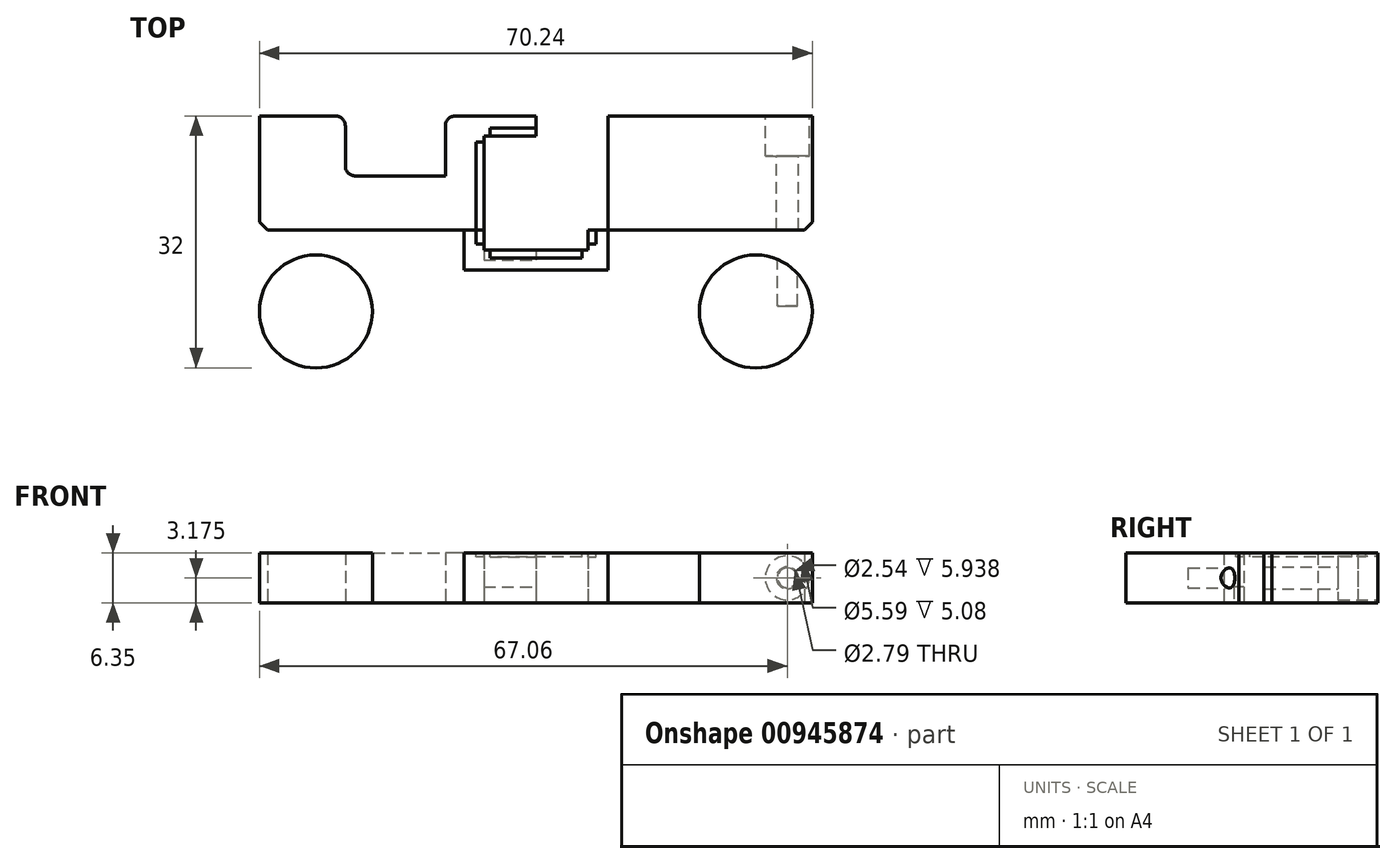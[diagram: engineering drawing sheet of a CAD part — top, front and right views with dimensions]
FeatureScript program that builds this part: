
annotation { "Feature Type Name" : "Feature", "Feature Type Description" : "" }
export const myFeature = defineFeature(function(context is Context, id is Id, definition is map)
    precondition{}
    {
        {
            var Q0;
            Q0=qCreatedBy(makeId("Top.planeOp"),FACE);
            var sketch = newSketch(context, id + "F0", { "sketchPlane" : qUnion([Q0])});
            skLineSegment(sketch, "E0", {"start": v(0, 0) * mm, "end": v(35.12, 0) * mm});
            skLineSegment(sketch, "E1", {"start": v(0, 0) * mm, "end": v(-35.12, 0) * mm});
            skLineSegment(sketch, "E2", {"start": v(0, 0) * mm, "end": v(0, -32) * mm});
            skLineSegment(sketch, "E3", {"start": v(0, 0) * mm, "end": v(0, -14.48) * mm});
            skLineSegment(sketch, "E4", {"start": v(35.12, 0) * mm, "end": v(35.12, -32) * mm});
            skLineSegment(sketch, "E5", {"start": v(-35.12, 0) * mm, "end": v(-35.12, -32) * mm});
            skLineSegment(sketch, "E6", {"start": v(-35.12, -32) * mm, "end": v(35.12, -32) * mm});
            skLineSegment(sketch, "E7", {"start": v(-35.12, -14.48) * mm, "end": v(-35.12, -15.5) * mm});
            skLineSegment(sketch, "E8", {"start": v(0, -32) * mm, "end": v(-27.94, -32) * mm});
            skLineSegment(sketch, "E9", {"start": v(0, -32) * mm, "end": v(27.94, -32) * mm});
            skLineSegment(sketch, "E10", {"start": v(-27.94, -32) * mm, "end": v(-27.94, -24.83) * mm});
            skLineSegment(sketch, "E11", {"start": v(27.94, -32) * mm, "end": v(27.94, -24.83) * mm});
            skCircle(sketch, "E12", {"center": v(-27.94, -24.83) * mm, "radius": 7.18 * mm});
            skCircle(sketch, "E13", {"center": v(27.94, -24.83) * mm, "radius": 7.18 * mm});
            skLineSegment(sketch, "E14", {"start": v(-35.12, 0) * mm, "end": v(-24.2, 0) * mm});
            skLineSegment(sketch, "E15", {"start": v(-24.2, 0) * mm, "end": v(-11.5, 0) * mm});
            skLineSegment(sketch, "E16", {"start": v(-11.5, 0) * mm, "end": v(-11.5, -7.62) * mm});
            skLineSegment(sketch, "E17.top", {"start": v(-24.2, -7.62) * mm, "end": v(-11.5, -7.62) * mm});
            skLineSegment(sketch, "E17.left", {"start": v(-24.2, 0) * mm, "end": v(-24.2, -7.62) * mm});
            skLineSegment(sketch, "E18", {"start": v(0, 0) * mm, "end": v(-6.6, 0) * mm});
            skLineSegment(sketch, "E19", {"start": v(-6.6, 0) * mm, "end": v(-9.14, 0) * mm});
            skLineSegment(sketch, "E20", {"start": v(-6.6, 0) * mm, "end": v(-6.6, -2.54) * mm});
            skLineSegment(sketch, "E21", {"start": v(-6.6, -2.54) * mm, "end": v(0, -2.54) * mm});
            skLineSegment(sketch, "E22", {"start": v(0, -2.54) * mm, "end": v(6.6, -2.54) * mm});
            skLineSegment(sketch, "E23", {"start": v(6.6, -2.54) * mm, "end": v(6.6, -17.02) * mm});
            skLineSegment(sketch, "E24.bottom", {"start": v(-6.6, -2.54) * mm, "end": v(6.6, -2.54) * mm});
            skLineSegment(sketch, "E24.top", {"start": v(-6.6, -17.02) * mm, "end": v(6.6, -17.02) * mm});
            skLineSegment(sketch, "E24.left", {"start": v(-6.6, -2.54) * mm, "end": v(-6.6, -17.02) * mm});
            skLineSegment(sketch, "E25.bottom", {"start": v(6.6, -17.02) * mm, "end": v(9.14, -17.02) * mm});
            skLineSegment(sketch, "E25.top", {"start": v(6.6, -19.56) * mm, "end": v(9.14, -19.56) * mm});
            skLineSegment(sketch, "E25.left", {"start": v(6.6, -17.02) * mm, "end": v(6.6, -19.56) * mm});
            skLineSegment(sketch, "E25.right", {"start": v(9.14, -17.02) * mm, "end": v(9.14, -19.56) * mm});
            skLineSegment(sketch, "E26.bottom", {"start": v(-9.14, 0) * mm, "end": v(9.14, 0) * mm});
            skLineSegment(sketch, "E26.top", {"start": v(-9.14, -19.56) * mm, "end": v(9.14, -19.56) * mm});
            skLineSegment(sketch, "E26.left", {"start": v(-9.14, 0) * mm, "end": v(-9.14, -19.56) * mm});
            skLineSegment(sketch, "E26.right", {"start": v(9.14, 0) * mm, "end": v(9.14, -19.56) * mm});
            skLineSegment(sketch, "E27", {"start": v(0, -14.48) * mm, "end": v(-35.12, -14.48) * mm});
            skLineSegment(sketch, "E28", {"start": v(0, -14.48) * mm, "end": v(35.12, -14.48) * mm});
            skLineSegment(sketch, "E29", {"start": v(35.12, -14.48) * mm, "end": v(35.12, -13.46) * mm});
            skLineSegment(sketch, "E30", {"start": v(-35.12, -14.48) * mm, "end": v(-34.1, -14.48) * mm});
            skLineSegment(sketch, "E31", {"start": v(35.12, -14.48) * mm, "end": v(34.1, -14.48) * mm});
            skLineSegment(sketch, "E32", {"start": v(-35.12, -13.46) * mm, "end": v(-34.1, -14.48) * mm});
            skLineSegment(sketch, "E33", {"start": v(-35.12, -15.5) * mm, "end": v(-34.1, -14.48) * mm});
            skLineSegment(sketch, "E34", {"start": v(34.1, -14.48) * mm, "end": v(35.12, -13.46) * mm});
            skLineSegment(sketch, "E35", {"start": v(35.12, -15.5) * mm, "end": v(34.1, -14.48) * mm});
            skLineSegment(sketch, "E36.top", {"start": v(-6.6, -18.29) * mm, "end": v(6.6, -18.29) * mm});
            skLineSegment(sketch, "E36.left", {"start": v(-6.6, -17.02) * mm, "end": v(-6.6, -18.29) * mm});
            skLineSegment(sketch, "E36.right", {"start": v(6.6, -17.02) * mm, "end": v(6.6, -18.29) * mm});
            skSolve(sketch);
        }
        {
            var Q0;
            {var subQ1=sQuery(id+"F0.wireOp",EDGE,"E1");Q0=makeQuery(id+"F0.imprint","IMPRINT",FACE,{"disambiguationData":[TD([[makeQuery(id+"F0.imprint","IMPRINT",EDGE,{"derivedFrom":subQ1}),1.0]])]});}
            var Q1;
            {var subQ1=sQuery(id+"F0.wireOp",EDGE,"E0");Q1=makeQuery(id+"F0.imprint","IMPRINT",FACE,{"disambiguationData":[TD([[makeQuery(id+"F0.imprint","IMPRINT",EDGE,{"derivedFrom":subQ1}),-1.0]])]});}
            var Q2;
            {var subQ5=sQuery(id+"F0.wireOp",EDGE,"E20");Q2=makeQuery(id+"F0.imprint","IMPRINT",FACE,{"disambiguationData":[TD([[makeQuery(id+"F0.imprint","IMPRINT",EDGE,{"derivedFrom":subQ5}),-1.0]])]});}
            var Q3;
            {var subQ5=sQuery(id+"F0.wireOp",EDGE,"E20");Q3=makeQuery(id+"F0.imprint","IMPRINT",FACE,{"disambiguationData":[TD([[makeQuery(id+"F0.imprint","IMPRINT",EDGE,{"derivedFrom":subQ5}),1.0]])]});}
            var Q4;
            {var subQ1=sQuery(id+"F0.wireOp",EDGE,"E26.bottom");var subQ3=sQuery(id+"F0.wireOp",EDGE,"E3");var subQ4=makeQuery(id+"F0.imprint","INTERSECT",VERTEX,{"derivedFrom":[subQ3,subQ1]});Q4=makeQuery(id+"F0.imprint","IMPRINT",FACE,{"disambiguationData":[TD([[makeQuery(id+"F0.imprint","IMPRINT",EDGE,{"disambiguationData":[TD([[subQ4,-1.0]])],"derivedFrom":subQ3}),1.0]])]});}
            extrude(context, id + "F1", {"entities" : qUnion([Q0, Q1, Q2, Q3, Q4]), "depth" : 6.35 * mm, "offsetDistance" : 25.4 * mm});
        }
        {
            var Q0;
            {var subQ0=sQuery(id+"F0.wireOp",EDGE,"E12");var subQ2=makeQuery(id+"F0.imprint","INTERSECT",VERTEX,{"derivedFrom":[sQuery(id+"F0.wireOp",EDGE,"E5"),subQ0]});Q0=makeQuery(id+"F0.imprint","IMPRINT",FACE,{"disambiguationData":[TD([[makeQuery(id+"F0.imprint","IMPRINT",EDGE,{"disambiguationData":[TD([[subQ2,-1.0]])],"derivedFrom":subQ0}),1.0]])]});}
            var Q1;
            {var subQ0=sQuery(id+"F0.wireOp",EDGE,"E13");var subQ2=makeQuery(id+"F0.imprint","INTERSECT",VERTEX,{"derivedFrom":[sQuery(id+"F0.wireOp",EDGE,"E4"),subQ0]});Q1=makeQuery(id+"F0.imprint","IMPRINT",FACE,{"disambiguationData":[TD([[makeQuery(id+"F0.imprint","IMPRINT",EDGE,{"disambiguationData":[TD([[subQ2,-1.0]])],"derivedFrom":subQ0}),1.0]])]});}
            var Q2;
            {var subQ6=sQuery(id+"F0.wireOp",EDGE,"E24.top");var subQ9=sQuery(id+"F0.wireOp",EDGE,"E2");var subQ10=makeQuery(id+"F0.imprint","INTERSECT",VERTEX,{"derivedFrom":[subQ9,subQ6]});Q2=makeQuery(id+"F0.imprint","IMPRINT",FACE,{"disambiguationData":[TD([[makeQuery(id+"F0.imprint","IMPRINT",EDGE,{"disambiguationData":[TD([[subQ10,-1.0]])],"derivedFrom":subQ9}),-1.0]])]});}
            var Q3;
            {var subQ1=sQuery(id+"F0.wireOp",EDGE,"E8");Q3=makeQuery(id+"F0.imprint","IMPRINT",FACE,{"disambiguationData":[TD([[makeQuery(id+"F0.imprint","IMPRINT",EDGE,{"derivedFrom":subQ1}),-1.0]])]});}
            var Q4;
            {var subQ0=sQuery(id+"F0.wireOp",EDGE,"Qt8gHTnX-YLuP-pRdt-GOWZ-hVGc7C5REt77.right");Q4=makeQuery(id+"F0.imprint","IMPRINT",FACE,{"disambiguationData":[TD([[makeQuery(id+"F0.imprint","IMPRINT",EDGE,{"derivedFrom":subQ0}),-1.0]])]});}
            var Q5;
            {var subQ0=sQuery(id+"F0.wireOp",EDGE,"E25.bottom");Q5=makeQuery(id+"F0.imprint","IMPRINT",FACE,{"disambiguationData":[TD([[makeQuery(id+"F0.imprint","IMPRINT",EDGE,{"derivedFrom":subQ0}),-1.0]])]});}
            var Q6;
            {var subQ0=sQuery(id+"F0.wireOp",EDGE,"E25.bottom");Q6=makeQuery(id+"F0.imprint","IMPRINT",FACE,{"disambiguationData":[TD([[makeQuery(id+"F0.imprint","IMPRINT",EDGE,{"derivedFrom":subQ0}),1.0]])]});}
            var Q7;
            {var subQ5=sQuery(id+"F0.wireOp",EDGE,"E25.left");Q7=makeQuery(id+"F0.imprint","IMPRINT",FACE,{"disambiguationData":[TD([[makeQuery(id+"F0.imprint","IMPRINT",EDGE,{"derivedFrom":subQ5}),-1.0]])]});}
            var Q8;
            {var subQ5=sQuery(id+"F0.wireOp",EDGE,"Qt8gHTnX-YLuP-pRdt-GOWZ-hVGc7C5REt77.left");Q8=makeQuery(id+"F0.imprint","IMPRINT",FACE,{"disambiguationData":[TD([[makeQuery(id+"F0.imprint","IMPRINT",EDGE,{"derivedFrom":subQ5}),1.0]])]});}
            var Q9;
            {var subQ1=sQuery(id+"F0.wireOp",EDGE,"E9");Q9=makeQuery(id+"F0.imprint","IMPRINT",FACE,{"disambiguationData":[TD([[makeQuery(id+"F0.imprint","IMPRINT",EDGE,{"derivedFrom":subQ1}),1.0]])]});}
            var Q10;
            {var subQ7=sQuery(id+"F0.wireOp",EDGE,"E36.left");Q10=makeQuery(id+"F0.imprint","IMPRINT",FACE,{"disambiguationData":[TD([[makeQuery(id+"F0.imprint","IMPRINT",EDGE,{"derivedFrom":subQ7}),-1.0]])]});}
            var Q11;
            {var subQ5=sQuery(id+"F0.wireOp",EDGE,"E36.right");Q11=makeQuery(id+"F0.imprint","IMPRINT",FACE,{"disambiguationData":[TD([[makeQuery(id+"F0.imprint","IMPRINT",EDGE,{"derivedFrom":subQ5}),-1.0]])]});}
            extrude(context, id + "F2", {"entities" : qUnion([Q0, Q1, Q2, Q3, Q4, Q5, Q6, Q7, Q8, Q9, Q10, Q11]), "depth" : 6.35 * mm, "offsetDistance" : 25.4 * mm});
        }
        {
            var Q0;
            {var subQ5=sQuery(id+"F0.wireOp",EDGE,"E36.right");Q0=makeQuery(id+"F0.imprint","IMPRINT",FACE,{"disambiguationData":[TD([[makeQuery(id+"F0.imprint","IMPRINT",EDGE,{"derivedFrom":subQ5}),-1.0]])]});}
            var Q1;
            {var subQ5=sQuery(id+"F0.wireOp",EDGE,"E36.left");Q1=makeQuery(id+"F0.imprint","IMPRINT",FACE,{"disambiguationData":[TD([[makeQuery(id+"F0.imprint","IMPRINT",EDGE,{"derivedFrom":subQ5}),1.0]])]});}
            extrude(context, id + "F3", {"entities" : qUnion([Q0, Q1]), "operationType" : NewBodyOperationType.REMOVE, "depth" : 2.03 * mm, "offsetDistance" : 25.4 * mm});
        }
        {
            var Q0;
            Q0=makeQuery(id+"F1.opExtrude","SWEPT_FACE",FACE,{"disambiguationData":[OSD([sQuery(id+"F0.wireOp",EDGE,"E14")])]});
            var sketch = newSketch(context, id + "F4", { "sketchPlane" : qUnion([Q0])});
            skLineSegment(sketch, "E37.bottom", {"start": v(35.12, 0) * mm, "end": v(28.77, 0) * mm});
            skLineSegment(sketch, "E37.top", {"start": v(35.12, 6.35) * mm, "end": v(28.77, 6.35) * mm});
            skLineSegment(sketch, "E37.left", {"start": v(35.12, 0) * mm, "end": v(35.12, 6.35) * mm});
            skLineSegment(sketch, "E37.right", {"start": v(28.77, 0) * mm, "end": v(28.77, 6.35) * mm});
            skLineSegment(sketch, "E38", {"start": v(28.77, 3.17) * mm, "end": v(35.12, 3.18) * mm});
            skCircle(sketch, "E39", {"center": v(31.94, 3.18) * mm, "radius": 2.8 * mm});
            skCircle(sketch, "E40", {"center": v(31.94, 3.18) * mm, "radius": 1.4 * mm});
            skCircle(sketch, "E41", {"center": v(31.94, 3.18) * mm, "radius": 1.27 * mm});
            skSolve(sketch);
        }
        {
            var Q0;
            Q0=makeQuery(id+"F1.opExtrude","SWEPT_FACE",FACE,{"disambiguationData":[OSD([sQuery(id+"F0.wireOp",EDGE,"E0"),sQuery(id+"F0.wireOp",EDGE,"E1"),sQuery(id+"F0.wireOp",EDGE,"E26.bottom")])]});
            var sketch = newSketch(context, id + "F5", { "sketchPlane" : qUnion([Q0])});
            skLineSegment(sketch, "E42.bottom", {"start": v(-35.12, 0) * mm, "end": v(-28.77, 0) * mm});
            skLineSegment(sketch, "E42.top", {"start": v(-35.12, 6.35) * mm, "end": v(-28.77, 6.35) * mm});
            skLineSegment(sketch, "E42.left", {"start": v(-35.12, 0) * mm, "end": v(-35.12, 6.35) * mm});
            skLineSegment(sketch, "E42.right", {"start": v(-28.77, 0) * mm, "end": v(-28.77, 6.35) * mm});
            skLineSegment(sketch, "E43", {"start": v(-35.12, 3.18) * mm, "end": v(-28.77, 3.18) * mm});
            skCircle(sketch, "E44", {"center": v(-31.94, 3.18) * mm, "radius": 2.8 * mm});
            skCircle(sketch, "E45", {"center": v(-31.94, 3.18) * mm, "radius": 1.4 * mm});
            skCircle(sketch, "E46", {"center": v(-31.94, 3.18) * mm, "radius": 1.27 * mm});
            skSolve(sketch);
        }
        {
            var Q0;
            {var subQ0=sQuery(id+"F5.wireOp",EDGE,"E44");var subQ1=sQuery(id+"F5.wireOp",EDGE,"E43");var subQ2=makeQuery(id+"F5.imprint","INTERSECT",VERTEX,{"disambiguationData":[OD(0.0)],"derivedFrom":[subQ1,subQ0]});Q0=makeQuery(id+"F5.imprint","IMPRINT",FACE,{"disambiguationData":[TD([[makeQuery(id+"F5.imprint","IMPRINT",EDGE,{"disambiguationData":[TD([[subQ2,-1.0]])],"derivedFrom":subQ1}),1.0]])]});}
            var Q1;
            {var subQ0=sQuery(id+"F5.wireOp",EDGE,"E44");var subQ1=sQuery(id+"F5.wireOp",EDGE,"E43");var subQ2=makeQuery(id+"F5.imprint","INTERSECT",VERTEX,{"disambiguationData":[OD(0.0)],"derivedFrom":[subQ1,subQ0]});Q1=makeQuery(id+"F5.imprint","IMPRINT",FACE,{"disambiguationData":[TD([[makeQuery(id+"F5.imprint","IMPRINT",EDGE,{"disambiguationData":[TD([[subQ2,-1.0]])],"derivedFrom":subQ1}),-1.0]])]});}
            var Q2;
            {var subQ0=sQuery(id+"F5.wireOp",EDGE,"E45");var subQ1=sQuery(id+"F5.wireOp",EDGE,"E43");var subQ2=makeQuery(id+"F5.imprint","INTERSECT",VERTEX,{"disambiguationData":[OD(0.0)],"derivedFrom":[subQ1,subQ0]});Q2=makeQuery(id+"F5.imprint","IMPRINT",FACE,{"disambiguationData":[TD([[makeQuery(id+"F5.imprint","IMPRINT",EDGE,{"disambiguationData":[TD([[subQ2,-1.0]])],"derivedFrom":subQ1}),-1.0]])]});}
            var Q3;
            {var subQ0=sQuery(id+"F5.wireOp",EDGE,"E46");var subQ1=sQuery(id+"F5.wireOp",EDGE,"E43");var subQ2=makeQuery(id+"F5.imprint","INTERSECT",VERTEX,{"disambiguationData":[OD(0.0)],"derivedFrom":[subQ1,subQ0]});Q3=makeQuery(id+"F5.imprint","IMPRINT",FACE,{"disambiguationData":[TD([[makeQuery(id+"F5.imprint","IMPRINT",EDGE,{"disambiguationData":[TD([[subQ2,-1.0]])],"derivedFrom":subQ1}),-1.0]])]});}
            var Q4;
            {var subQ0=sQuery(id+"F5.wireOp",EDGE,"E45");var subQ1=sQuery(id+"F5.wireOp",EDGE,"E43");var subQ2=makeQuery(id+"F5.imprint","INTERSECT",VERTEX,{"disambiguationData":[OD(0.0)],"derivedFrom":[subQ1,subQ0]});Q4=makeQuery(id+"F5.imprint","IMPRINT",FACE,{"disambiguationData":[TD([[makeQuery(id+"F5.imprint","IMPRINT",EDGE,{"disambiguationData":[TD([[subQ2,-1.0]])],"derivedFrom":subQ1}),1.0]])]});}
            var Q5;
            {var subQ0=sQuery(id+"F5.wireOp",EDGE,"E46");var subQ1=sQuery(id+"F5.wireOp",EDGE,"E43");var subQ2=makeQuery(id+"F5.imprint","INTERSECT",VERTEX,{"disambiguationData":[OD(0.0)],"derivedFrom":[subQ1,subQ0]});Q5=makeQuery(id+"F5.imprint","IMPRINT",FACE,{"disambiguationData":[TD([[makeQuery(id+"F5.imprint","IMPRINT",EDGE,{"disambiguationData":[TD([[subQ2,-1.0]])],"derivedFrom":subQ1}),1.0]])]});}
            var Q6;
            {var subQ0=sQuery(id+"F4.wireOp",EDGE,"E39");var subQ1=sQuery(id+"F4.wireOp",EDGE,"E38");var subQ2=makeQuery(id+"F4.imprint","INTERSECT",VERTEX,{"disambiguationData":[OD(0.0)],"derivedFrom":[subQ1,subQ0]});Q6=makeQuery(id+"F4.imprint","IMPRINT",FACE,{"disambiguationData":[TD([[makeQuery(id+"F4.imprint","IMPRINT",EDGE,{"disambiguationData":[TD([[subQ2,-1.0]])],"derivedFrom":subQ1}),1.0]])]});}
            var Q7;
            {var subQ0=sQuery(id+"F4.wireOp",EDGE,"E39");var subQ1=sQuery(id+"F4.wireOp",EDGE,"E38");var subQ2=makeQuery(id+"F4.imprint","INTERSECT",VERTEX,{"disambiguationData":[OD(0.0)],"derivedFrom":[subQ1,subQ0]});Q7=makeQuery(id+"F4.imprint","IMPRINT",FACE,{"disambiguationData":[TD([[makeQuery(id+"F4.imprint","IMPRINT",EDGE,{"disambiguationData":[TD([[subQ2,-1.0]])],"derivedFrom":subQ1}),-1.0]])]});}
            var Q8;
            {var subQ0=sQuery(id+"F4.wireOp",EDGE,"E40");var subQ1=sQuery(id+"F4.wireOp",EDGE,"E38");var subQ2=makeQuery(id+"F4.imprint","INTERSECT",VERTEX,{"disambiguationData":[OD(0.0)],"derivedFrom":[subQ1,subQ0]});Q8=makeQuery(id+"F4.imprint","IMPRINT",FACE,{"disambiguationData":[TD([[makeQuery(id+"F4.imprint","IMPRINT",EDGE,{"disambiguationData":[TD([[subQ2,-1.0]])],"derivedFrom":subQ1}),-1.0]])]});}
            var Q9;
            {var subQ0=sQuery(id+"F4.wireOp",EDGE,"E40");var subQ1=sQuery(id+"F4.wireOp",EDGE,"E38");var subQ2=makeQuery(id+"F4.imprint","INTERSECT",VERTEX,{"disambiguationData":[OD(0.0)],"derivedFrom":[subQ1,subQ0]});Q9=makeQuery(id+"F4.imprint","IMPRINT",FACE,{"disambiguationData":[TD([[makeQuery(id+"F4.imprint","IMPRINT",EDGE,{"disambiguationData":[TD([[subQ2,-1.0]])],"derivedFrom":subQ1}),1.0]])]});}
            var Q10;
            {var subQ0=sQuery(id+"F4.wireOp",EDGE,"E41");var subQ1=sQuery(id+"F4.wireOp",EDGE,"E38");var subQ2=makeQuery(id+"F4.imprint","INTERSECT",VERTEX,{"disambiguationData":[OD(0.0)],"derivedFrom":[subQ1,subQ0]});Q10=makeQuery(id+"F4.imprint","IMPRINT",FACE,{"disambiguationData":[TD([[makeQuery(id+"F4.imprint","IMPRINT",EDGE,{"disambiguationData":[TD([[subQ2,-1.0]])],"derivedFrom":subQ1}),1.0]])]});}
            var Q11;
            {var subQ0=sQuery(id+"F4.wireOp",EDGE,"E41");var subQ1=sQuery(id+"F4.wireOp",EDGE,"E38");var subQ2=makeQuery(id+"F4.imprint","INTERSECT",VERTEX,{"disambiguationData":[OD(0.0)],"derivedFrom":[subQ1,subQ0]});Q11=makeQuery(id+"F4.imprint","IMPRINT",FACE,{"disambiguationData":[TD([[makeQuery(id+"F4.imprint","IMPRINT",EDGE,{"disambiguationData":[TD([[subQ2,-1.0]])],"derivedFrom":subQ1}),-1.0]])]});}
            extrude(context, id + "F6", {"entities" : qUnion([Q0, Q1, Q2, Q3, Q4, Q5, Q6, Q7, Q8, Q9, Q10, Q11]), "operationType" : NewBodyOperationType.REMOVE, "oppositeDirection" : true, "depth" : 5.08 * mm, "offsetDistance" : 25.4 * mm});
        }
        {
            var Q0;
            {var subQ0=sQuery(id+"F5.wireOp",EDGE,"E46");var subQ1=sQuery(id+"F5.wireOp",EDGE,"E43");var subQ2=makeQuery(id+"F5.imprint","INTERSECT",VERTEX,{"disambiguationData":[OD(0.0)],"derivedFrom":[subQ1,subQ0]});Q0=makeQuery(id+"F5.imprint","IMPRINT",FACE,{"disambiguationData":[TD([[makeQuery(id+"F5.imprint","IMPRINT",EDGE,{"disambiguationData":[TD([[subQ2,-1.0]])],"derivedFrom":subQ1}),1.0]])]});}
            var Q1;
            {var subQ0=sQuery(id+"F5.wireOp",EDGE,"E46");var subQ1=sQuery(id+"F5.wireOp",EDGE,"E43");var subQ2=makeQuery(id+"F5.imprint","INTERSECT",VERTEX,{"disambiguationData":[OD(0.0)],"derivedFrom":[subQ1,subQ0]});Q1=makeQuery(id+"F5.imprint","IMPRINT",FACE,{"disambiguationData":[TD([[makeQuery(id+"F5.imprint","IMPRINT",EDGE,{"disambiguationData":[TD([[subQ2,-1.0]])],"derivedFrom":subQ1}),-1.0]])]});}
            var Q2;
            {var subQ0=sQuery(id+"F4.wireOp",EDGE,"E41");var subQ1=sQuery(id+"F4.wireOp",EDGE,"E38");var subQ2=makeQuery(id+"F4.imprint","INTERSECT",VERTEX,{"disambiguationData":[OD(0.0)],"derivedFrom":[subQ1,subQ0]});Q2=makeQuery(id+"F4.imprint","IMPRINT",FACE,{"disambiguationData":[TD([[makeQuery(id+"F4.imprint","IMPRINT",EDGE,{"disambiguationData":[TD([[subQ2,-1.0]])],"derivedFrom":subQ1}),1.0]])]});}
            var Q3;
            {var subQ0=sQuery(id+"F4.wireOp",EDGE,"E41");var subQ1=sQuery(id+"F4.wireOp",EDGE,"E38");var subQ2=makeQuery(id+"F4.imprint","INTERSECT",VERTEX,{"disambiguationData":[OD(0.0)],"derivedFrom":[subQ1,subQ0]});Q3=makeQuery(id+"F4.imprint","IMPRINT",FACE,{"disambiguationData":[TD([[makeQuery(id+"F4.imprint","IMPRINT",EDGE,{"disambiguationData":[TD([[subQ2,-1.0]])],"derivedFrom":subQ1}),-1.0]])]});}
            extrude(context, id + "F7", {"entities" : qUnion([Q0, Q1, Q2, Q3]), "operationType" : NewBodyOperationType.REMOVE, "oppositeDirection" : true, "depth" : 24.13 * mm, "offsetDistance" : 25.4 * mm});
        }
        {
            var Q0;
            {var subQ0=sQuery(id+"F5.wireOp",EDGE,"E45");var subQ1=sQuery(id+"F5.wireOp",EDGE,"E43");var subQ2=makeQuery(id+"F5.imprint","INTERSECT",VERTEX,{"disambiguationData":[OD(0.0)],"derivedFrom":[subQ1,subQ0]});Q0=makeQuery(id+"F5.imprint","IMPRINT",FACE,{"disambiguationData":[TD([[makeQuery(id+"F5.imprint","IMPRINT",EDGE,{"disambiguationData":[TD([[subQ2,-1.0]])],"derivedFrom":subQ1}),1.0]])]});}
            var Q1;
            {var subQ0=sQuery(id+"F5.wireOp",EDGE,"E45");var subQ1=sQuery(id+"F5.wireOp",EDGE,"E43");var subQ2=makeQuery(id+"F5.imprint","INTERSECT",VERTEX,{"disambiguationData":[OD(0.0)],"derivedFrom":[subQ1,subQ0]});Q1=makeQuery(id+"F5.imprint","IMPRINT",FACE,{"disambiguationData":[TD([[makeQuery(id+"F5.imprint","IMPRINT",EDGE,{"disambiguationData":[TD([[subQ2,-1.0]])],"derivedFrom":subQ1}),-1.0]])]});}
            var Q2;
            {var subQ0=sQuery(id+"F4.wireOp",EDGE,"E41");var subQ1=sQuery(id+"F4.wireOp",EDGE,"E38");var subQ2=makeQuery(id+"F4.imprint","INTERSECT",VERTEX,{"disambiguationData":[OD(0.0)],"derivedFrom":[subQ1,subQ0]});Q2=makeQuery(id+"F4.imprint","IMPRINT",FACE,{"disambiguationData":[TD([[makeQuery(id+"F4.imprint","IMPRINT",EDGE,{"disambiguationData":[TD([[subQ2,-1.0]])],"derivedFrom":subQ1}),1.0]])]});}
            var Q3;
            {var subQ0=sQuery(id+"F4.wireOp",EDGE,"E41");var subQ1=sQuery(id+"F4.wireOp",EDGE,"E38");var subQ2=makeQuery(id+"F4.imprint","INTERSECT",VERTEX,{"disambiguationData":[OD(0.0)],"derivedFrom":[subQ1,subQ0]});Q3=makeQuery(id+"F4.imprint","IMPRINT",FACE,{"disambiguationData":[TD([[makeQuery(id+"F4.imprint","IMPRINT",EDGE,{"disambiguationData":[TD([[subQ2,-1.0]])],"derivedFrom":subQ1}),-1.0]])]});}
            var Q4;
            Q4=makeQuery(id+"F1.opExtrude","SWEPT_FACE",FACE,{"disambiguationData":[OSD([sQuery(id+"F0.wireOp",EDGE,"E27")])]});
            extrude(context, id + "F8", {"entities" : qUnion([Q0, Q1, Q2, Q3]), "operationType" : NewBodyOperationType.REMOVE, "endBound" : BoundingType.UP_TO_SURFACE, "oppositeDirection" : true, "depth" : 25.4 * mm, "endBoundEntityFace" : qUnion([Q4]), "offsetDistance" : 25.4 * mm});
        }
        {
            var Q0;
            Q0=makeQuery(id+"F1.opExtrude","CAP_FACE",FACE,{"disambiguationData":[OSD([sQuery(id+"F0.wireOp",EDGE,"E0"),sQuery(id+"F0.wireOp",EDGE,"E1"),sQuery(id+"F0.wireOp",EDGE,"E4"),sQuery(id+"F0.wireOp",EDGE,"E5"),sQuery(id+"F0.wireOp",EDGE,"E14"),sQuery(id+"F0.wireOp",EDGE,"E17.top"),sQuery(id+"F0.wireOp",EDGE,"E17.left"),sQuery(id+"F0.wireOp",EDGE,"E16"),sQuery(id+"F0.wireOp",EDGE,"E24.bottom"),sQuery(id+"F0.wireOp",EDGE,"E24.left"),sQuery(id+"F0.wireOp",EDGE,"E23"),sQuery(id+"F0.wireOp",EDGE,"E26.bottom"),sQuery(id+"F0.wireOp",EDGE,"E27"),sQuery(id+"F0.wireOp",EDGE,"E28"),sQuery(id+"F0.wireOp",EDGE,"E32"),sQuery(id+"F0.wireOp",EDGE,"E34")])],"isStart":false});
            var sketch = newSketch(context, id + "F9", { "sketchPlane" : qUnion([Q0])});
            skLineSegment(sketch, "E47", {"start": v(0, -2.54) * mm, "end": v(-5.84, -2.54) * mm});
            skLineSegment(sketch, "E48", {"start": v(0, -2.54) * mm, "end": v(5.84, -2.54) * mm});
            skLineSegment(sketch, "E49", {"start": v(0, -2.54) * mm, "end": v(0, -2.03) * mm});
            skLineSegment(sketch, "E50.bottom", {"start": v(5.84, -2.54) * mm, "end": v(-5.84, -2.54) * mm});
            skLineSegment(sketch, "E50.top", {"start": v(5.84, -1.52) * mm, "end": v(-5.84, -1.52) * mm});
            skLineSegment(sketch, "E50.left", {"start": v(5.84, -2.54) * mm, "end": v(5.84, -1.52) * mm});
            skLineSegment(sketch, "E50.right", {"start": v(-5.84, -2.54) * mm, "end": v(-5.84, -1.52) * mm});
            skPoint(sketch, "E50.middle", {"position": v(0, -2.03) * mm});
            skSolve(sketch);
        }
        {
            var Q0;
            Q0=makeQuery(id+"F2.opExtrude","CAP_FACE",FACE,{"disambiguationData":[OSD([sQuery(id+"F0.wireOp",EDGE,"E4"),sQuery(id+"F0.wireOp",EDGE,"E5"),sQuery(id+"F0.wireOp",EDGE,"E8"),sQuery(id+"F0.wireOp",EDGE,"E9"),sQuery(id+"F0.wireOp",EDGE,"E12"),sQuery(id+"F0.wireOp",EDGE,"E13"),sQuery(id+"F0.wireOp",EDGE,"E24.left"),sQuery(id+"F0.wireOp",EDGE,"E23"),sQuery(id+"F0.wireOp",EDGE,"E27"),sQuery(id+"F0.wireOp",EDGE,"E28"),sQuery(id+"F0.wireOp",EDGE,"E33"),sQuery(id+"F0.wireOp",EDGE,"E35"),sQuery(id+"F0.wireOp",EDGE,"E24.top")])],"isStart":false});
            var sketch = newSketch(context, id + "F10", { "sketchPlane" : qUnion([Q0])});
            skLineSegment(sketch, "E51", {"start": v(0, -17.02) * mm, "end": v(0, -17.53) * mm});
            skLineSegment(sketch, "E52.bottom", {"start": v(5.84, -17.02) * mm, "end": v(-5.84, -17.02) * mm});
            skLineSegment(sketch, "E52.top", {"start": v(5.84, -18.03) * mm, "end": v(-5.84, -18.03) * mm});
            skLineSegment(sketch, "E52.left", {"start": v(5.84, -17.02) * mm, "end": v(5.84, -18.03) * mm});
            skLineSegment(sketch, "E52.right", {"start": v(-5.84, -17.02) * mm, "end": v(-5.84, -18.03) * mm});
            skPoint(sketch, "E52.middle", {"position": v(0, -17.53) * mm});
            skSolve(sketch);
        }
        {
            var Q0;
            Q0=makeQuery(id+"F9.imprint","IMPRINT",FACE,{"disambiguationData":[TD([[makeQuery(id+"F9.imprint","IMPRINT",EDGE,{"derivedFrom":sQuery(id+"F9.wireOp",EDGE,"E50.top")}),-1.0]])]});
            var sketch = newSketch(context, id + "F11", { "sketchPlane" : qUnion([Q0])});
            skLineSegment(sketch, "E53", {"start": v(0, 0) * mm, "end": v(0, -2.54) * mm});
            skLineSegment(sketch, "E54", {"start": v(0, -2.54) * mm, "end": v(0, -17.02) * mm});
            skLineSegment(sketch, "E55", {"start": v(0, -9.78) * mm, "end": v(6.6, -9.78) * mm});
            skLineSegment(sketch, "E56", {"start": v(0, -9.78) * mm, "end": v(-6.6, -9.78) * mm});
            skLineSegment(sketch, "E57", {"start": v(-6.6, -9.78) * mm, "end": v(-7.11, -9.78) * mm});
            skLineSegment(sketch, "E58", {"start": v(6.6, -9.78) * mm, "end": v(7.11, -9.78) * mm});
            skLineSegment(sketch, "E59.bottom", {"start": v(-6.6, -16.26) * mm, "end": v(-7.62, -16.26) * mm});
            skLineSegment(sketch, "E59.top", {"start": v(-6.6, -3.3) * mm, "end": v(-7.62, -3.3) * mm});
            skLineSegment(sketch, "E59.left", {"start": v(-6.6, -16.26) * mm, "end": v(-6.6, -3.3) * mm});
            skLineSegment(sketch, "E59.right", {"start": v(-7.62, -16.26) * mm, "end": v(-7.62, -3.3) * mm});
            skPoint(sketch, "E59.middle", {"position": v(-7.11, -9.78) * mm});
            skLineSegment(sketch, "E60.bottom", {"start": v(6.6, -3.3) * mm, "end": v(7.62, -3.3) * mm});
            skLineSegment(sketch, "E60.top", {"start": v(6.6, -16.26) * mm, "end": v(7.62, -16.26) * mm});
            skLineSegment(sketch, "E60.left", {"start": v(6.6, -3.3) * mm, "end": v(6.6, -16.26) * mm});
            skLineSegment(sketch, "E60.right", {"start": v(7.62, -3.3) * mm, "end": v(7.62, -16.26) * mm});
            skPoint(sketch, "E60.middle", {"position": v(7.11, -9.78) * mm});
            skSolve(sketch);
        }
        {
            var Q0;
            Q0=makeQuery(id+"F9.imprint","IMPRINT",FACE,{"disambiguationData":[TD([[makeQuery(id+"F9.imprint","IMPRINT",EDGE,{"derivedFrom":sQuery(id+"F9.wireOp",EDGE,"E50.top")}),1.0]])]});
            var Q1;
            Q1=makeQuery(id+"F10.imprint","IMPRINT",FACE,{"disambiguationData":[TD([[makeQuery(id+"F10.imprint","IMPRINT",EDGE,{"derivedFrom":sQuery(id+"F10.wireOp",EDGE,"E52.top")}),-1.0]])]});
            var Q2;
            {var subQ0=sQuery(id+"F11.wireOp",EDGE,"E59.bottom");Q2=makeQuery(id+"F11.imprint","IMPRINT",FACE,{"disambiguationData":[TD([[makeQuery(id+"F11.imprint","IMPRINT",EDGE,{"derivedFrom":subQ0}),-1.0]])]});}
            var Q3;
            {var subQ0=sQuery(id+"F11.wireOp",EDGE,"E60.top");Q3=makeQuery(id+"F11.imprint","IMPRINT",FACE,{"disambiguationData":[TD([[makeQuery(id+"F11.imprint","IMPRINT",EDGE,{"derivedFrom":subQ0}),1.0]])]});}
            extrude(context, id + "F12", {"entities" : qUnion([Q0, Q1, Q2, Q3]), "operationType" : NewBodyOperationType.REMOVE, "oppositeDirection" : true, "depth" : 0.5 * mm, "offsetDistance" : 25.4 * mm});
        }
        {
            var Q0;
            {var subQ4=sQuery(id+"F11.wireOp",EDGE,"E59.top");Q0=makeQuery(id+"F11.imprint","IMPRINT",FACE,{"disambiguationData":[TD([[makeQuery(id+"F11.imprint","IMPRINT",EDGE,{"derivedFrom":subQ4}),1.0]])]});}
            var Q1;
            {var subQ4=sQuery(id+"F11.wireOp",EDGE,"E60.bottom");Q1=makeQuery(id+"F11.imprint","IMPRINT",FACE,{"disambiguationData":[TD([[makeQuery(id+"F11.imprint","IMPRINT",EDGE,{"derivedFrom":subQ4}),-1.0]])]});}
            extrude(context, id + "F13", {"entities" : qUnion([Q0, Q1]), "operationType" : NewBodyOperationType.REMOVE, "oppositeDirection" : true, "depth" : 0.5 * mm, "offsetDistance" : 25.4 * mm});
        }
        {
            var Q0;
            Q0=makeQuery(id+"F1.opExtrude","SWEPT_EDGE",EDGE,{"disambiguationData":[OSD([sQuery(id+"F0.wireOp",EDGE,"E1"),sQuery(id+"F0.wireOp",EDGE,"E15"),sQuery(id+"F0.wireOp",EDGE,"E16")])]});
            var Q1;
            Q1=makeQuery(id+"F1.opExtrude","SWEPT_EDGE",EDGE,{"disambiguationData":[OSD([sQuery(id+"F0.wireOp",EDGE,"E14"),sQuery(id+"F0.wireOp",EDGE,"E15"),sQuery(id+"F0.wireOp",EDGE,"E17.left")])]});
            fillet(context, id + "F14", {"entities" : qUnion([Q0, Q1]), "radius" : 1.27 * mm, "tangentPropagation" : true, "allowEdgeOverflow" : false});
        }
    });
